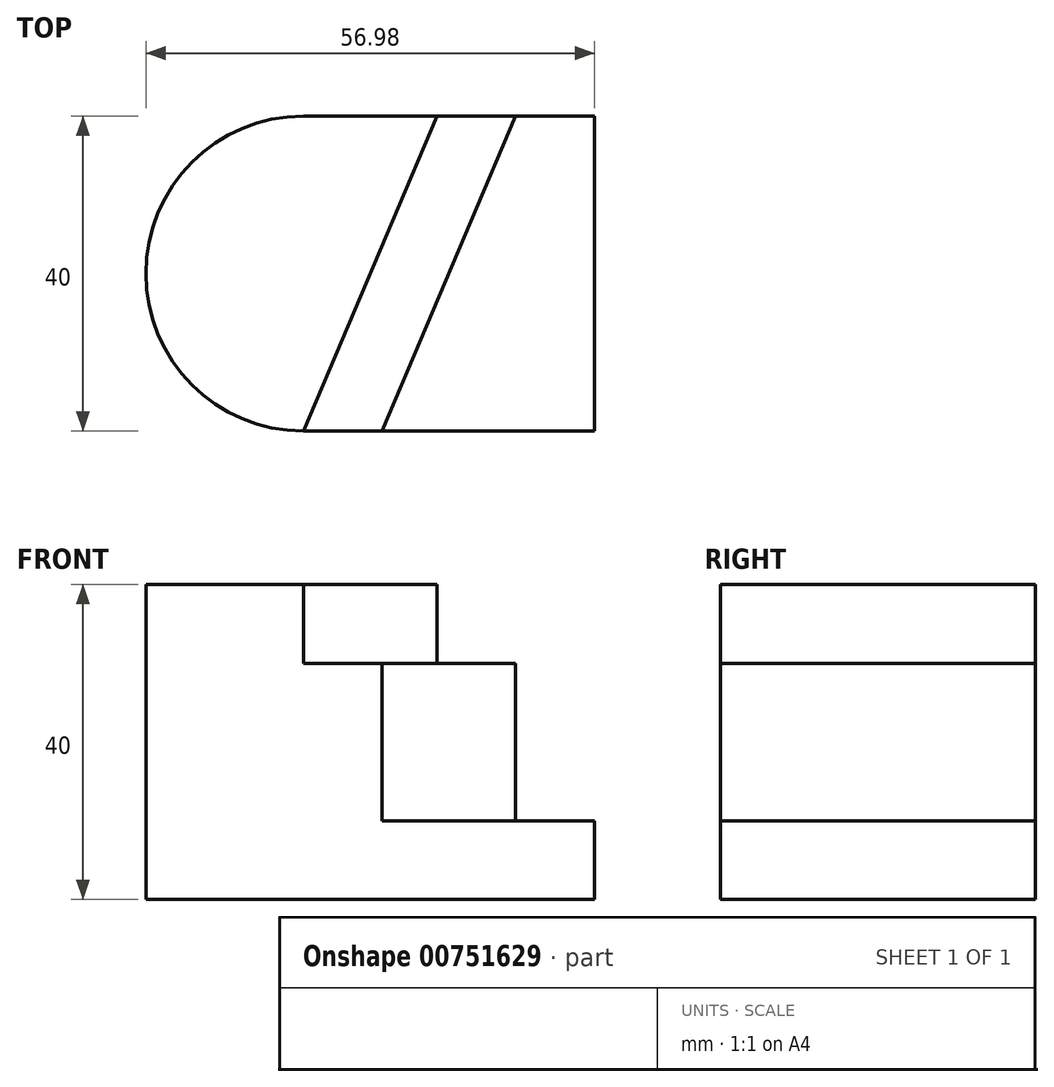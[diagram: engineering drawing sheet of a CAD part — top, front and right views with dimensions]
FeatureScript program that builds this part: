
annotation { "Feature Type Name" : "Feature", "Feature Type Description" : "" }
export const myFeature = defineFeature(function(context is Context, id is Id, definition is map)
    precondition{}
    {
        {
            var Q0;
            Q0=qCreatedBy(makeId("Front.planeOp"),FACE);
            var sketch = newSketch(context, id + "F0", { "sketchPlane" : qUnion([Q0])});
            skLineSegment(sketch, "E0.bottom", {"start": v(0, 0) * mm, "end": v(60, 0) * mm});
            skLineSegment(sketch, "E0.top", {"start": v(0, 40) * mm, "end": v(60, 40) * mm});
            skLineSegment(sketch, "E0.left", {"start": v(0, 0) * mm, "end": v(0, 40) * mm});
            skLineSegment(sketch, "E0.right", {"start": v(60, 0) * mm, "end": v(60, 40) * mm});
            skSolve(sketch);
        }
        {
            var Q0;
            Q0=makeQuery(id+"F0.imprint","IMPRINT",FACE,{"disambiguationData":[TD([[makeQuery(id+"F0.imprint","IMPRINT",EDGE,{"derivedFrom":sQuery(id+"F0.wireOp",EDGE,"E0.bottom")}),1.0]])]});
            extrude(context, id + "F1", {"entities" : qUnion([Q0]), "depth" : 40 * mm, "offsetDistance" : 25 * mm});
        }
        {
            var Q0;
            Q0=makeQuery(id+"F1.opExtrude","SWEPT_FACE",FACE,{"disambiguationData":[OSD([sQuery(id+"F0.wireOp",EDGE,"E0.top")])]});
            var sketch = newSketch(context, id + "F2", { "sketchPlane" : qUnion([Q0])});
            skArc(sketch, "E1", {"start": v(23.02, 0) * mm, "mid": v(3.02, -20) * mm, "end": v(23.02, -40) * mm});
            skSolve(sketch);
        }
        {
            var Q0;
            Q0 = qSketchRegion(id + "F2", true);
            var Q1;
            {var subQ0=sQuery(id+"F2.wireOp",EDGE,"E1");Q1=makeQuery(id+"F2.imprint","IMPRINT",FACE,{"disambiguationData":[TD([[makeQuery(id+"F2.imprint","IMPRINT",EDGE,{"derivedFrom":subQ0}),-1.0]])]});}
            extrude(context, id + "F3", {"entities" : qUnion([Q0, Q1]), "operationType" : NewBodyOperationType.REMOVE, "oppositeDirection" : true, "depth" : 40 * mm, "offsetDistance" : 25 * mm});
        }
        {
            var Q0;
            Q0=makeQuery(id+"F1.opExtrude","SWEPT_FACE",FACE,{"disambiguationData":[OSD([sQuery(id+"F0.wireOp",EDGE,"E0.top")])]});
            var sketch = newSketch(context, id + "F4", { "sketchPlane" : qUnion([Q0])});
            skLineSegment(sketch, "E2", {"start": v(23.02, -40) * mm, "end": v(33.02, -40) * mm});
            skLineSegment(sketch, "E3", {"start": v(23.02, -40) * mm, "end": v(40, 0) * mm});
            skLineSegment(sketch, "E4", {"start": v(33.02, -40) * mm, "end": v(50, 0) * mm});
            skLineSegment(sketch, "E5", {"start": v(40, 0) * mm, "end": v(50, 0) * mm});
            skLineSegment(sketch, "E6", {"start": v(33.02, -40) * mm, "end": v(60, -40) * mm});
            skLineSegment(sketch, "E7", {"start": v(60, -40) * mm, "end": v(60, 0) * mm});
            skLineSegment(sketch, "E8", {"start": v(60, 0) * mm, "end": v(50, 0) * mm});
            skLineSegment(sketch, "E9", {"start": v(50, 0) * mm, "end": v(60, 0) * mm});
            skLineSegment(sketch, "E10", {"start": v(40, 0) * mm, "end": v(30, 0) * mm});
            skSolve(sketch);
        }
        {
            var Q0;
            Q0=makeQuery(id+"F4.imprint","IMPRINT",FACE,{"disambiguationData":[TD([[makeQuery(id+"F4.imprint","IMPRINT",EDGE,{"derivedFrom":sQuery(id+"F4.wireOp",EDGE,"E4")}),-1.0]])]});
            extrude(context, id + "F5", {"entities" : qUnion([Q0]), "operationType" : NewBodyOperationType.REMOVE, "oppositeDirection" : true, "depth" : 30 * mm, "offsetDistance" : 25 * mm});
        }
        {
            var Q0;
            Q0=makeQuery(id+"F1.opExtrude","SWEPT_FACE",FACE,{"disambiguationData":[OSD([sQuery(id+"F0.wireOp",EDGE,"E0.top")])]});
            var sketch = newSketch(context, id + "F6", { "sketchPlane" : qUnion([Q0])});
            skLineSegment(sketch, "E11", {"start": v(23.02, -40) * mm, "end": v(40, 0) * mm});
            skLineSegment(sketch, "E12", {"start": v(40, 0) * mm, "end": v(50, 0) * mm});
            skSolve(sketch);
        }
        {
            var Q0;
            Q0 = qSketchRegion(id + "F6", true);
            var Q1;
            Q1=makeQuery(id+"F6.imprint","IMPRINT",FACE,{"disambiguationData":[TD([[makeQuery(id+"F6.imprint","IMPRINT",EDGE,{"derivedFrom":sQuery(id+"F6.wireOp",EDGE,"E11")}),-1.0]])]});
            extrude(context, id + "F7", {"entities" : qUnion([Q0, Q1]), "operationType" : NewBodyOperationType.REMOVE, "oppositeDirection" : true, "depth" : 10 * mm, "offsetDistance" : 25 * mm});
        }
    });
